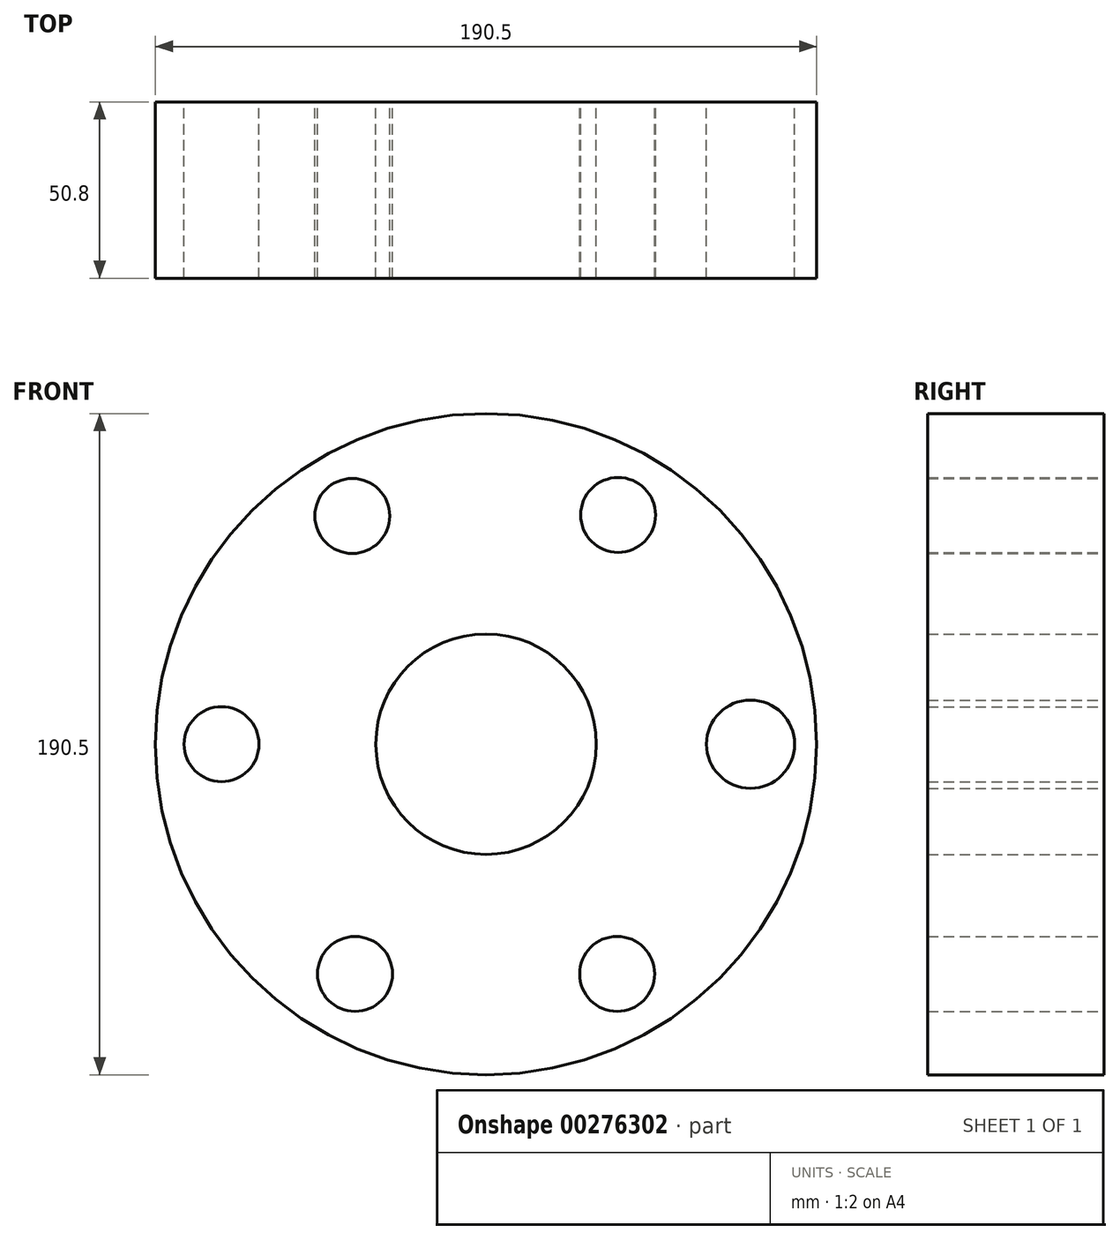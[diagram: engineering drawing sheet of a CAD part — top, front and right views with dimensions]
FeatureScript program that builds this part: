
annotation { "Feature Type Name" : "Feature", "Feature Type Description" : "" }
export const myFeature = defineFeature(function(context is Context, id is Id, definition is map)
    precondition{}
    {
        {
            var Q0;
            Q0=qCreatedBy(makeId("Front.planeOp"),FACE);
            var sketch = newSketch(context, id + "F0", { "sketchPlane" : qUnion([Q0])});
            skCircle(sketch, "E0", {"center": v(0, 0) * mm, "radius": 76.2 * mm});
            skCircle(sketch, "E1", {"center": v(0, 0) * mm, "radius": 31.75 * mm});
            skCircle(sketch, "E2", {"center": v(38.04, 66.02) * mm, "radius": 10.8 * mm});
            skCircle(sketch, "E3", {"center": v(-38.53, 65.74) * mm, "radius": 10.8 * mm});
            skCircle(sketch, "E4", {"center": v(-76.2, 0) * mm, "radius": 10.8 * mm});
            skCircle(sketch, "E5", {"center": v(-37.74, -66.2) * mm, "radius": 10.8 * mm});
            skCircle(sketch, "E6", {"center": v(37.76, -66.19) * mm, "radius": 10.8 * mm});
            skCircle(sketch, "E7", {"center": v(76.2, 0) * mm, "radius": 12.7 * mm});
            skCircle(sketch, "E8", {"center": v(0, 0) * mm, "radius": 95.25 * mm});
            skCircle(sketch, "E9", {"center": v(0, 0) * mm, "radius": 99.7 * mm});
            skSolve(sketch);
        }
        {
            var Q0;
            Q0=makeQuery(id+"F0.imprint","IMPRINT",FACE,{"disambiguationData":[TD([[makeQuery(id+"F0.imprint","IMPRINT",EDGE,{"derivedFrom":sQuery(id+"F0.wireOp",EDGE,"E8")}),1.0]])]});
            var Q1;
            Q1=makeQuery(id+"F0.imprint","IMPRINT",FACE,{"disambiguationData":[TD([[makeQuery(id+"F0.imprint","IMPRINT",EDGE,{"derivedFrom":sQuery(id+"F0.wireOp",EDGE,"E1")}),-1.0]])]});
            extrude(context, id + "F1", {"entities" : qUnion([Q0, Q1]), "depth" : 50.8 * mm});
        }
    });
